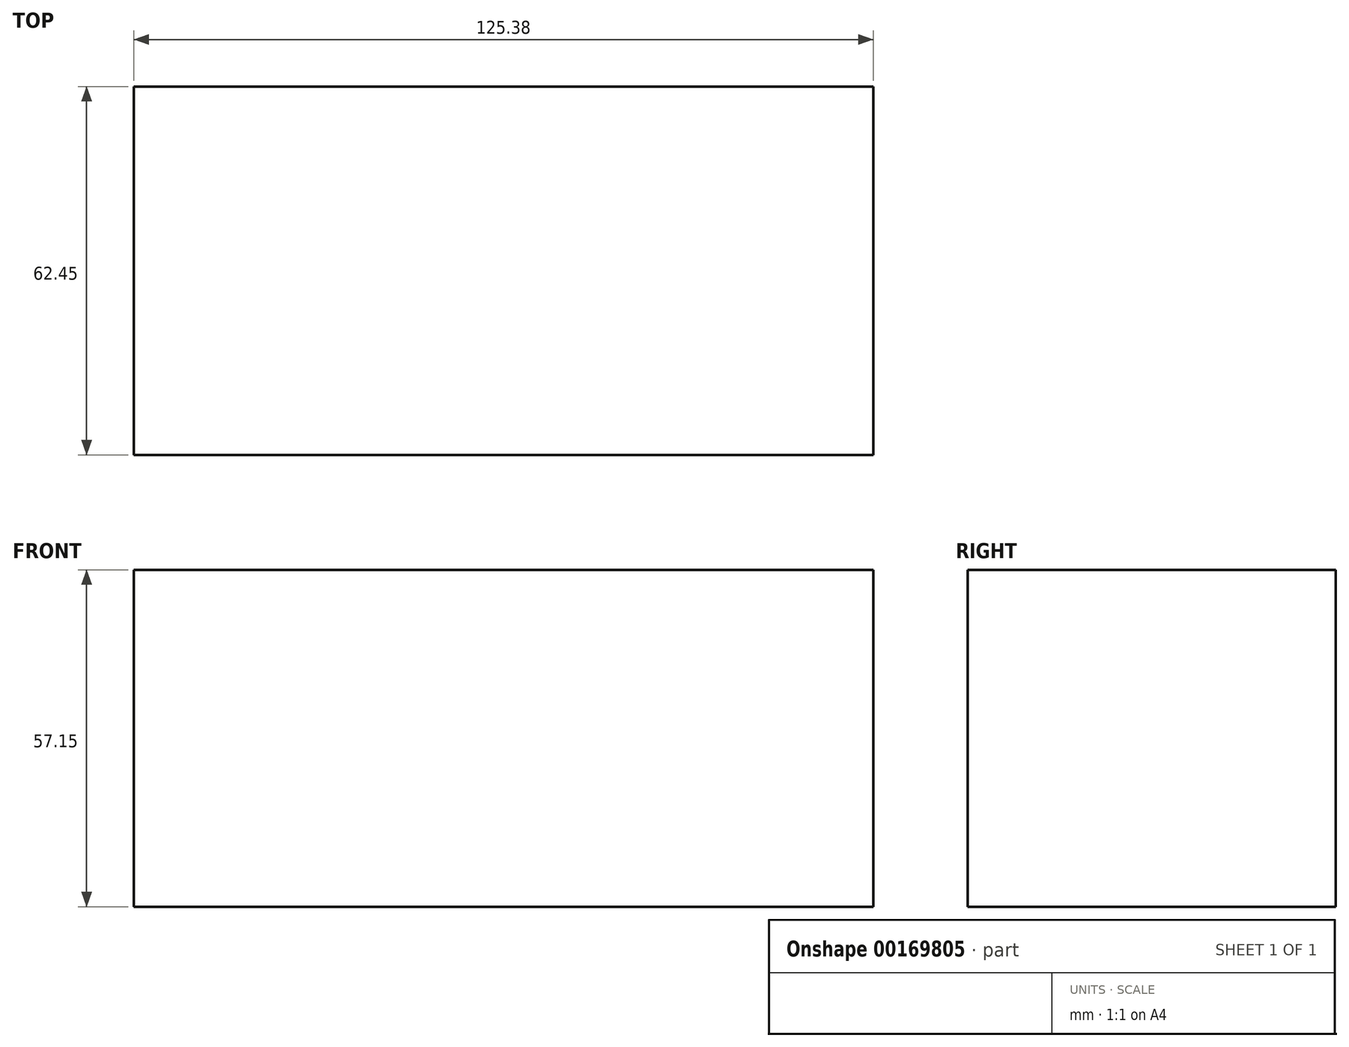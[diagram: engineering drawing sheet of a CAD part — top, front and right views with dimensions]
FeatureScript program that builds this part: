
annotation { "Feature Type Name" : "Feature", "Feature Type Description" : "" }
export const myFeature = defineFeature(function(context is Context, id is Id, definition is map)
    precondition{}
    {
        {
            var Q0;
            Q0=qCreatedBy(makeId("Top.planeOp"),FACE);
            var sketch = newSketch(context, id + "F0", { "sketchPlane" : qUnion([Q0])});
            skLineSegment(sketch, "E0.bottom", {"start": v(0, 0) * mm, "end": v(-125.38, 0) * mm});
            skLineSegment(sketch, "E0.top", {"start": v(0, 62.45) * mm, "end": v(-125.38, 62.45) * mm});
            skLineSegment(sketch, "E0.left", {"start": v(0, 0) * mm, "end": v(0, 62.45) * mm});
            skLineSegment(sketch, "E0.right", {"start": v(-125.38, 0) * mm, "end": v(-125.38, 62.45) * mm});
            skSolve(sketch);
        }
        {
            var Q0;
            Q0=makeQuery(id+"F0.imprint","IMPRINT",FACE,{"disambiguationData":[TD([[makeQuery(id+"F0.imprint","IMPRINT",EDGE,{"derivedFrom":sQuery(id+"F0.wireOp",EDGE,"E0.bottom")}),-1.0]])]});
            extrude(context, id + "F1", {"entities" : qUnion([Q0]), "depth" : 57.15 * mm});
        }
    });
